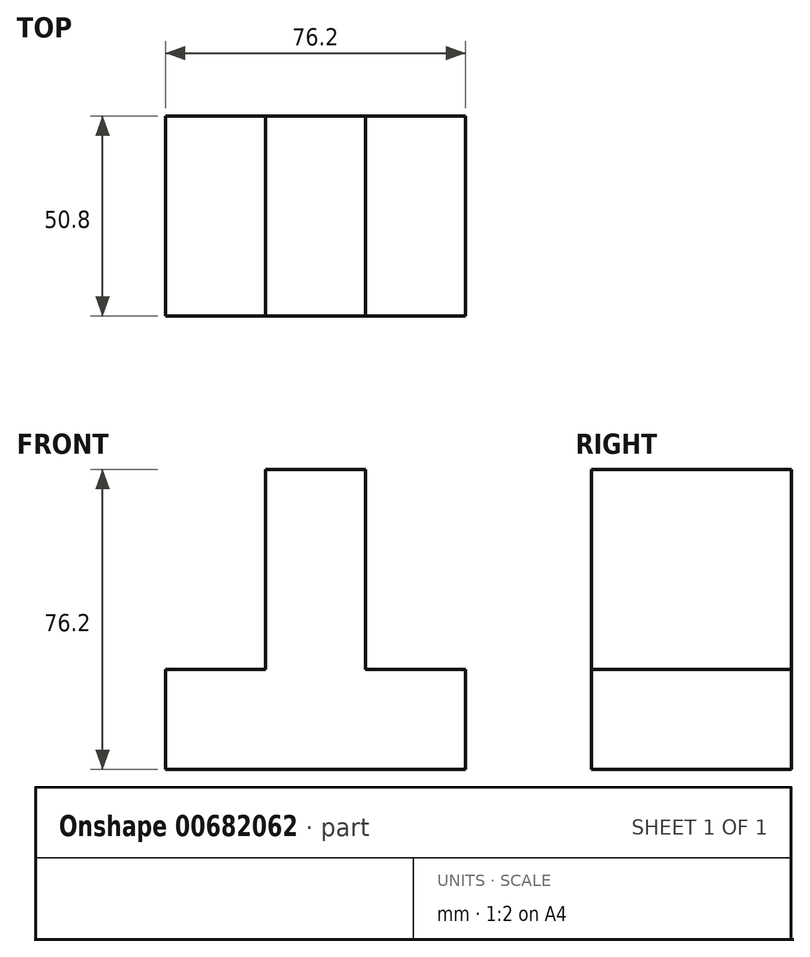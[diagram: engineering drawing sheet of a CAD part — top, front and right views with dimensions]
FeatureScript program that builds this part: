
annotation { "Feature Type Name" : "Feature", "Feature Type Description" : "" }
export const myFeature = defineFeature(function(context is Context, id is Id, definition is map)
    precondition{}
    {
        {
            var Q0;
            Q0=qCreatedBy(makeId("Front.planeOp"),FACE);
            var sketch = newSketch(context, id + "F0", { "sketchPlane" : qUnion([Q0])});
            skLineSegment(sketch, "E0", {"start": v(-24.92, -21.48) * mm, "end": v(51.28, -21.48) * mm});
            skLineSegment(sketch, "E1", {"start": v(-24.92, -21.48) * mm, "end": v(-24.92, 3.92) * mm});
            skLineSegment(sketch, "E2", {"start": v(-24.92, 3.92) * mm, "end": v(0.48, 3.92) * mm});
            skLineSegment(sketch, "E3", {"start": v(0.48, 3.92) * mm, "end": v(0.48, 54.72) * mm});
            skLineSegment(sketch, "E4", {"start": v(0.48, 54.72) * mm, "end": v(25.88, 54.72) * mm});
            skLineSegment(sketch, "E5", {"start": v(25.88, 54.72) * mm, "end": v(25.88, 3.92) * mm});
            skLineSegment(sketch, "E6", {"start": v(25.88, 3.92) * mm, "end": v(51.28, 3.92) * mm});
            skLineSegment(sketch, "E7", {"start": v(51.28, 3.92) * mm, "end": v(51.28, -21.48) * mm});
            skSolve(sketch);
        }
        {
            var Q0;
            Q0 = qSketchRegion(id + "F0", true);
            extrude(context, id + "F1", {"entities" : qUnion([Q0]), "depth" : 50.8 * mm, "offsetDistance" : 25.4 * mm});
        }
    });
